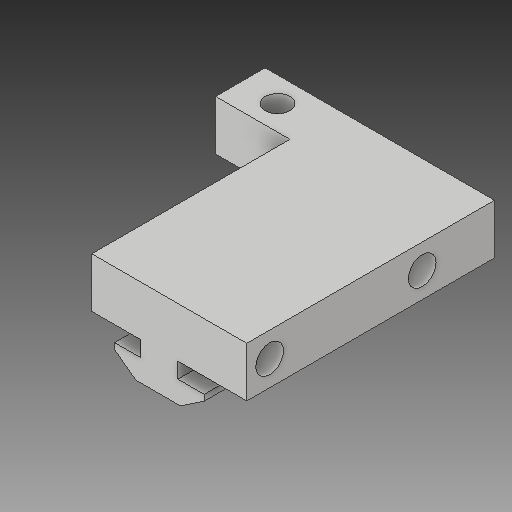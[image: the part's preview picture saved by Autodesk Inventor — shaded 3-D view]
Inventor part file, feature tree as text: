
AUTODESK INVENTOR PART (.ipt)
format: ipt  version: 2017 (Build 210142000, 142)  size: 183,808 bytes
history: native  units: in
note: dims shown in document units (in); Inventor stores cm internally (conversion verified against a paired STEP export)
features: sketch x6, projected_geometry x5, extrude x4, hole x2
ambient origin geometry x8: Origin, YZ Plane, XZ Plane, XY Plane, X Axis, Y Axis, Z Axis, Center Point
bodies: Solid1 (feature_tree)
feature tree (17):
  extrude  "Extrusion1"  Depth=0.0787in
  extrude  "Extrusion6"  Depth=0.115in
  extrude  "Extrusion9"  Depth=0.03in
  hole  "Hole11"  [1 undecoded]
  extrude  "Extrusion10"  Depth=0.1325in
  hole  "Hole12"  [1 undecoded]
  sketch  "Sketch1"  dims[d0=0.6693in d2=0.1969in d3=0.0787in]
  sketch  "Sketch14"  dims[d6=0.4524in d7=0.115in]
  projected_geometry  "Projected Loop4"
  sketch  "Sketch17"  dims[d8=0.225in d9=0.2221in d11=0.03in]
  projected_geometry  "Projected Loop7"
  sketch  "Sketch19"  dims[d12=0.03in d13=1.0in d14=0.0in]
  projected_geometry  "Projected Loop9"
  sketch  "Sketch20"  dims[d78=0.215in d88=0.1325in]
  projected_geometry  "Projected Loop10"
  sketch  "Sketch21"  dims[d89=0.1325in d161=0.25in d162=0.375in d163=0.0in d175=0.25in d176=0.055in d177=0.0in d190=0.125in d191=0.75in d192=0.375in d193=0.25in d194=0.5635in d195=1.0in d196=0.8108in d197=0.25in d198=0.0in d199=1.25in d200=0.77in d201=0.365in d202=0.125in d203=0.125in d204=0.14in d205=0.75in d206=0.375in d207=0.25in d208=0.5635in d209=1.0in d210=0.8108in d71=1.0in d72=1.0in d112=1.0in d113=1.0in]
  projected_geometry  "Projected Loop11"
note: 2 required parameter values undecoded (feature->parameter linkage not recoverable at this tier; creation-order binding heuristic only, values carry confidence <= 0.55)
